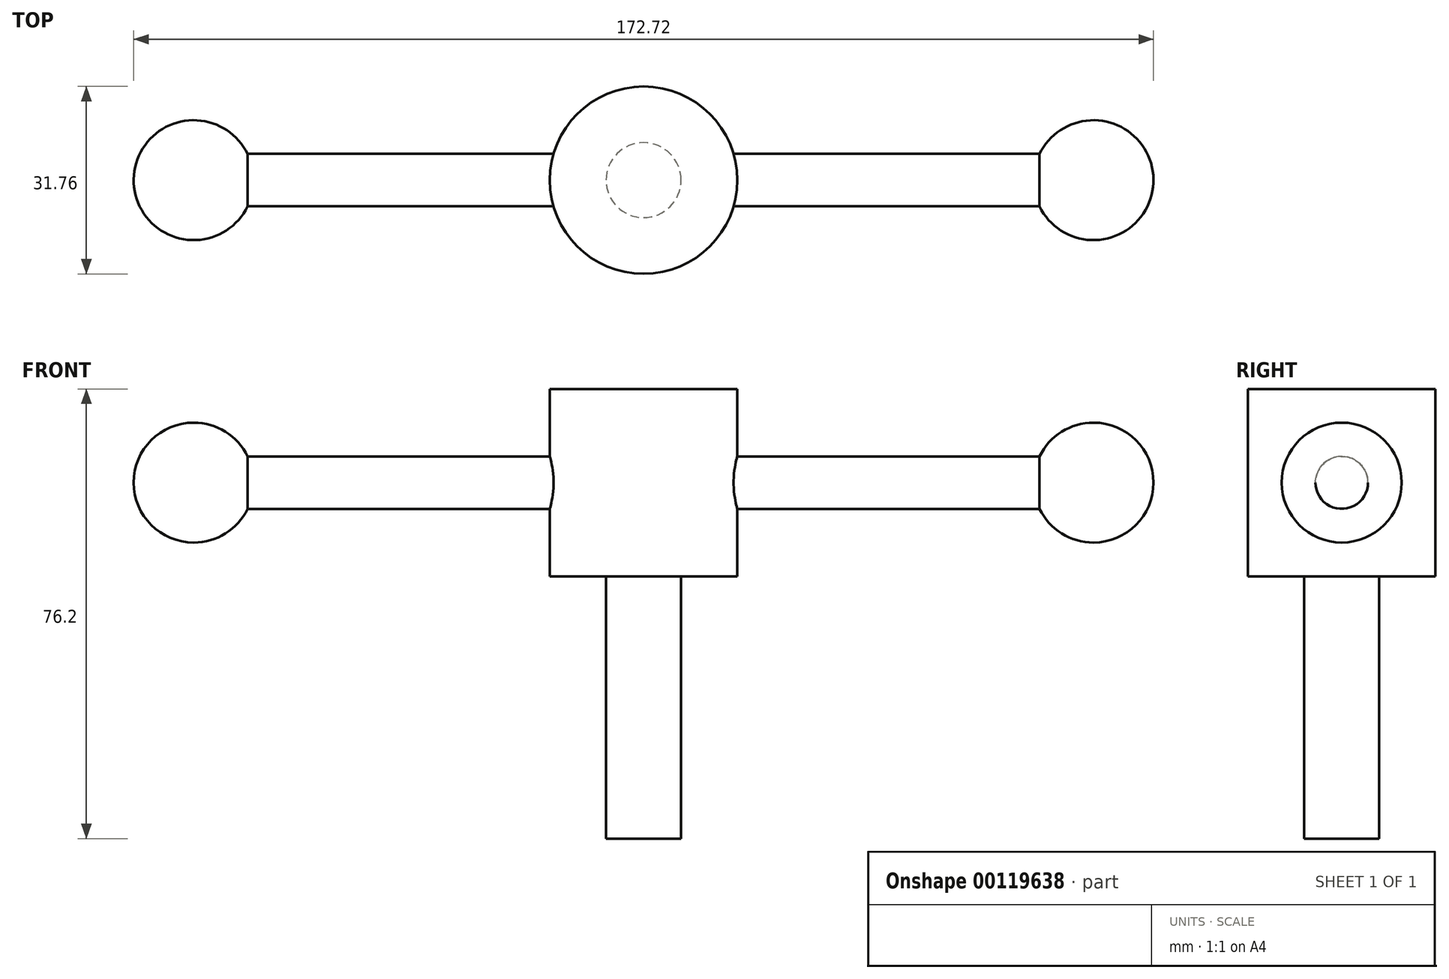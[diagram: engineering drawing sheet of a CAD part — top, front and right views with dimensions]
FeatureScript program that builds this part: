
annotation { "Feature Type Name" : "Feature", "Feature Type Description" : "" }
export const myFeature = defineFeature(function(context is Context, id is Id, definition is map)
    precondition{}
    {
        {
            var Q0;
            Q0=qCreatedBy(makeId("Top.planeOp"),FACE);
            var sketch = newSketch(context, id + "F0", { "sketchPlane" : qUnion([Q0])});
            skCircle(sketch, "E0", {"center": v(0, 0) * mm, "radius": 15.88 * mm});
            skSolve(sketch);
        }
        {
            var Q0;
            Q0 = qSketchRegion(id + "F0", true);
            extrude(context, id + "F1", {"entities" : qUnion([Q0]), "oppositeDirection" : true, "depth" : 31.75 * mm});
        }
        {
            var Q0;
            Q0=makeQuery(id+"F1.opExtrude","CAP_FACE",FACE,{"disambiguationData":[OSD([sQuery(id+"F0.wireOp",EDGE,"E0")])],"isStart":false});
            var sketch = newSketch(context, id + "F2", { "sketchPlane" : qUnion([Q0])});
            skCircle(sketch, "E1", {"center": v(0, 0) * mm, "radius": 6.35 * mm});
            skSolve(sketch);
        }
        {
            var Q0;
            Q0 = qSketchRegion(id + "F2", true);
            extrude(context, id + "F3", {"entities" : qUnion([Q0]), "operationType" : NewBodyOperationType.ADD, "depth" : 44.45 * mm});
        }
        {
            var Q0;
            Q0=qCreatedBy(makeId("Right.planeOp"),FACE);
            var sketch = newSketch(context, id + "F4", { "sketchPlane" : qUnion([Q0])});
            skLineSegment(sketch, "E2", {"start": v(0, 0) * mm, "end": v(0, -15.88) * mm, "construction": true});
            skCircle(sketch, "E3", {"center": v(0, -15.88) * mm, "radius": 4.45 * mm});
            skSolve(sketch);
        }
        {
            var Q0;
            Q0 = qSketchRegion(id + "F4", true);
            extrude(context, id + "F5", {"entities" : qUnion([Q0]), "operationType" : NewBodyOperationType.ADD, "endBound" : BoundingType.SYMMETRIC, "depth" : 152.4 * mm});
        }
        {
            var Q0;
            Q0=makeQuery(id+"F5.opExtrude","CAP_FACE",FACE,{"disambiguationData":[OSD([sQuery(id+"F4.wireOp",EDGE,"E3")])],"isStart":false});
            var sketch = newSketch(context, id + "F6", { "sketchPlane" : qUnion([Q0])});
            skLineSegment(sketch, "E4", {"start": v(0, -15.88) * mm, "end": v(0, -5.71) * mm});
            skLineSegment(sketch, "E5", {"start": v(0, -15.88) * mm, "end": v(0, -26.04) * mm});
            skArc(sketch, "E6", {"start": v(0, -26.04) * mm, "mid": v(10.16, -15.88) * mm, "end": v(0, -5.71) * mm});
            skSolve(sketch);
        }
        {
            var Q0;
            Q0 = qSketchRegion(id + "F6", true);
            var Q1;
            Q1=sQuery(id+"F6.wireOp",EDGE,"E4");
            revolve(context, id + "F7", {"operationType" : NewBodyOperationType.ADD, "entities" : qUnion([Q0]), "axis" : qUnion([Q1]), "revolveType" : RevolveType.FULL});
        }
        {
            var Q0;
            Q0=makeQuery(id+"F5.opExtrude","CAP_FACE",FACE,{"disambiguationData":[OSD([sQuery(id+"F4.wireOp",EDGE,"E3")])],"isStart":true});
            var sketch = newSketch(context, id + "F8", { "sketchPlane" : qUnion([Q0])});
            skLineSegment(sketch, "E7", {"start": v(0, -15.88) * mm, "end": v(0, -5.71) * mm});
            skLineSegment(sketch, "E8", {"start": v(0, -15.88) * mm, "end": v(0, -26.04) * mm});
            skArc(sketch, "E9", {"start": v(0, -5.71) * mm, "mid": v(10.16, -15.88) * mm, "end": v(0, -26.04) * mm});
            skSolve(sketch);
        }
        {
            var Q0;
            Q0 = qSketchRegion(id + "F8", true);
            var Q1;
            Q1=sQuery(id+"F8.wireOp",EDGE,"E7");
            revolve(context, id + "F9", {"operationType" : NewBodyOperationType.ADD, "entities" : qUnion([Q0]), "axis" : qUnion([Q1]), "revolveType" : RevolveType.FULL});
        }
    });
